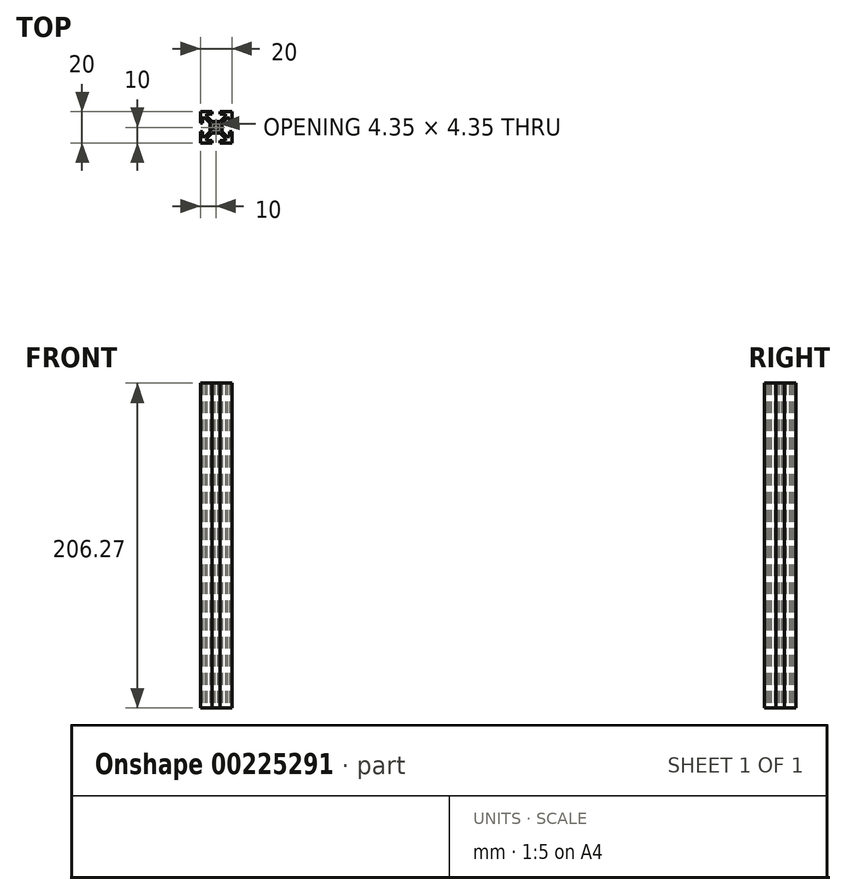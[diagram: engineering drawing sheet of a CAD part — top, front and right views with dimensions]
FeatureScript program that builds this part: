
annotation { "Feature Type Name" : "Feature", "Feature Type Description" : "" }
export const myFeature = defineFeature(function(context is Context, id is Id, definition is map)
    precondition{}
    {
        {
            var Q0;
            Q0=qCreatedBy(makeId("Top.planeOp"),FACE);
            var sketch = newSketch(context, id + "F0", { "sketchPlane" : qUnion([Q0])});
            skLineSegment(sketch, "E0.bottom", {"start": v(10, 10) * mm, "end": v(-10, 10) * mm});
            skLineSegment(sketch, "E0.top", {"start": v(10, -10) * mm, "end": v(-10, -10) * mm});
            skLineSegment(sketch, "E0.left", {"start": v(10, 10) * mm, "end": v(10, -10) * mm});
            skLineSegment(sketch, "E0.right", {"start": v(-10, 10) * mm, "end": v(-10, -10) * mm});
            skPoint(sketch, "E0.middle", {"position": v(0, 0) * mm});
            skLineSegment(sketch, "E1", {"start": v(-10, 10) * mm, "end": v(10, -10) * mm, "construction": true});
            skLineSegment(sketch, "E2", {"start": v(-10, -10) * mm, "end": v(10, 10) * mm, "construction": true});
            skLineSegment(sketch, "E3", {"start": v(0, 10) * mm, "end": v(0, -10) * mm, "construction": true});
            skLineSegment(sketch, "E4", {"start": v(-10, 0) * mm, "end": v(10, 0) * mm, "construction": true});
            skPoint(sketch, "E4.endSnap0", {"position": v(10, 0) * mm});
            skLineSegment(sketch, "E5", {"start": v(-2.63, 13.49) * mm, "end": v(2.63, 13.49) * mm});
            skLineSegment(sketch, "E6", {"start": v(2.63, 13.49) * mm, "end": v(2.63, 8.5) * mm});
            skLineSegment(sketch, "E7", {"start": v(2.63, 8.5) * mm, "end": v(6, 8.5) * mm});
            skLineSegment(sketch, "E8", {"start": v(6, 8.5) * mm, "end": v(6, 7.06) * mm});
            skLineSegment(sketch, "E9", {"start": v(6, 7.06) * mm, "end": v(2.6, 3.66) * mm});
            skLineSegment(sketch, "E10", {"start": v(2.6, 3.66) * mm, "end": v(-2.6, 3.66) * mm});
            skLineSegment(sketch, "E11", {"start": v(-2.6, 3.66) * mm, "end": v(-6, 7.06) * mm});
            skLineSegment(sketch, "E12", {"start": v(-6, 7.06) * mm, "end": v(-6, 8.5) * mm});
            skLineSegment(sketch, "E13", {"start": v(-6, 8.5) * mm, "end": v(-2.63, 8.5) * mm});
            skLineSegment(sketch, "E14", {"start": v(-2.63, 8.5) * mm, "end": v(-2.63, 13.49) * mm});
            skCircle(sketch, "E15", {"center": v(0, 0) * mm, "radius": 2.1 * mm});
            skLineSegment(sketch, "E16.MirrorCS", {"start": v(-7.06, 6) * mm, "end": v(-8.5, 6) * mm});
            skLineSegment(sketch, "E17.MirrorCS", {"start": v(-3.66, 2.6) * mm, "end": v(-7.06, 6) * mm});
            skLineSegment(sketch, "E18.MirrorCS", {"start": v(-8.5, 6) * mm, "end": v(-8.5, 2.63) * mm});
            skLineSegment(sketch, "E19.MirrorCS", {"start": v(-3.66, -2.6) * mm, "end": v(-3.66, 2.6) * mm});
            skLineSegment(sketch, "E20.MirrorCS", {"start": v(-7.06, -6) * mm, "end": v(-3.66, -2.6) * mm});
            skLineSegment(sketch, "E21.MirrorCS", {"start": v(-8.5, -6) * mm, "end": v(-7.06, -6) * mm});
            skLineSegment(sketch, "E22.MirrorCS", {"start": v(-8.5, -2.63) * mm, "end": v(-8.5, -6) * mm});
            skLineSegment(sketch, "E23.MirrorCS", {"start": v(-13.49, -2.63) * mm, "end": v(-8.5, -2.63) * mm});
            skLineSegment(sketch, "E24.MirrorCS", {"start": v(-13.49, 2.63) * mm, "end": v(-13.49, -2.63) * mm});
            skLineSegment(sketch, "E25.MirrorCS", {"start": v(-8.5, 2.63) * mm, "end": v(-13.49, 2.63) * mm});
            skLineSegment(sketch, "E26.MirrorCS", {"start": v(-2.6, -3.66) * mm, "end": v(-6, -7.06) * mm});
            skLineSegment(sketch, "E27.MirrorCS", {"start": v(2.6, -3.66) * mm, "end": v(-2.6, -3.66) * mm});
            skLineSegment(sketch, "E28.MirrorCS", {"start": v(6, -7.06) * mm, "end": v(2.6, -3.66) * mm});
            skLineSegment(sketch, "E29.MirrorCS", {"start": v(6, -8.5) * mm, "end": v(6, -7.06) * mm});
            skLineSegment(sketch, "E30.MirrorCS", {"start": v(2.63, -8.5) * mm, "end": v(6, -8.5) * mm});
            skLineSegment(sketch, "E31.MirrorCS", {"start": v(2.63, -13.49) * mm, "end": v(2.63, -8.5) * mm});
            skLineSegment(sketch, "E32.MirrorCS", {"start": v(-2.63, -13.49) * mm, "end": v(2.63, -13.49) * mm});
            skLineSegment(sketch, "E33.MirrorCS", {"start": v(-2.63, -8.5) * mm, "end": v(-2.63, -13.49) * mm});
            skLineSegment(sketch, "E34.MirrorCS", {"start": v(-6, -8.5) * mm, "end": v(-2.63, -8.5) * mm});
            skLineSegment(sketch, "E35.MirrorCS", {"start": v(-6, -7.06) * mm, "end": v(-6, -8.5) * mm});
            skLineSegment(sketch, "E36.MirrorCS", {"start": v(7.06, 6) * mm, "end": v(3.66, 2.6) * mm});
            skLineSegment(sketch, "E37.MirrorCS", {"start": v(8.5, 6) * mm, "end": v(7.06, 6) * mm});
            skLineSegment(sketch, "E38.MirrorCS", {"start": v(8.5, 2.63) * mm, "end": v(8.5, 6) * mm});
            skLineSegment(sketch, "E39.MirrorCS", {"start": v(13.49, 2.63) * mm, "end": v(8.5, 2.63) * mm});
            skLineSegment(sketch, "E40.MirrorCS", {"start": v(13.49, -2.63) * mm, "end": v(13.49, 2.63) * mm});
            skLineSegment(sketch, "E41.MirrorCS", {"start": v(8.5, -2.63) * mm, "end": v(13.49, -2.63) * mm});
            skLineSegment(sketch, "E42.MirrorCS", {"start": v(8.5, -6) * mm, "end": v(8.5, -2.63) * mm});
            skLineSegment(sketch, "E43.MirrorCS", {"start": v(7.06, -6) * mm, "end": v(8.5, -6) * mm});
            skLineSegment(sketch, "E44.MirrorCS", {"start": v(3.66, -2.6) * mm, "end": v(7.06, -6) * mm});
            skLineSegment(sketch, "E45.MirrorCS", {"start": v(3.66, 2.6) * mm, "end": v(3.66, -2.6) * mm});
            skCircle(sketch, "E46", {"center": v(-1.48, 1.48) * mm, "radius": 0.7 * mm});
            skCircle(sketch, "E47.MirrorC", {"center": v(1.48, 1.48) * mm, "radius": 0.7 * mm});
            skCircle(sketch, "E48.MirrorC", {"center": v(-1.48, -1.48) * mm, "radius": 0.7 * mm});
            skCircle(sketch, "E49.MirrorC", {"center": v(1.48, -1.48) * mm, "radius": 0.7 * mm});
            skSolve(sketch);
        }
        {
            var Q0;
            {var subQ29=sQuery(id+"F0.wireOp",EDGE,"E7");Q0=makeQuery(id+"F0.imprint","IMPRINT",FACE,{"disambiguationData":[TD([[makeQuery(id+"F0.imprint","IMPRINT",EDGE,{"derivedFrom":subQ29}),1.0]])]});}
            extrude(context, id + "F1", {"entities" : qUnion([Q0]), "depth" : 206.27 * mm});
        }
    });
